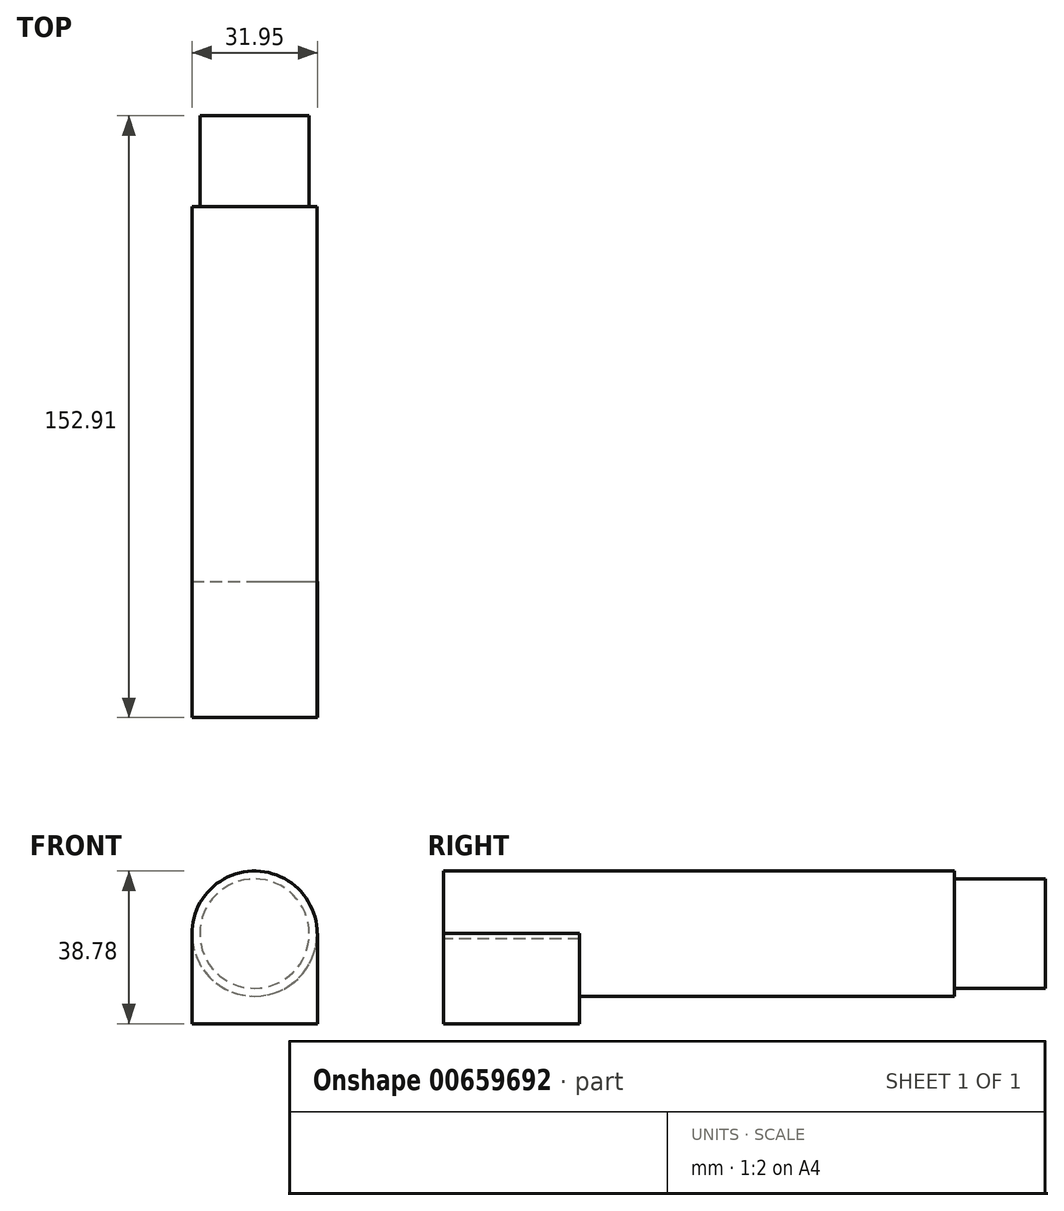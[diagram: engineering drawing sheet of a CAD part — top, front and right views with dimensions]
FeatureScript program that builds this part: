
annotation { "Feature Type Name" : "Feature", "Feature Type Description" : "" }
export const myFeature = defineFeature(function(context is Context, id is Id, definition is map)
    precondition{}
    {
        {
            var Q0;
            Q0=qCreatedBy(makeId("Front.planeOp"),FACE);
            var sketch = newSketch(context, id + "F0", { "sketchPlane" : qUnion([Q0])});
            skCircle(sketch, "E0", {"center": v(0, 0) * mm, "radius": 15.9 * mm});
            skSolve(sketch);
        }
        {
            var Q0;
            Q0 = qSketchRegion(id + "F0", true);
            extrude(context, id + "F1", {"entities" : qUnion([Q0]), "oppositeDirection" : true, "depth" : 129.8 * mm, "offsetDistance" : 25.4 * mm});
        }
        {
            var Q0;
            Q0=qCreatedBy(makeId("Front.planeOp"),FACE);
            var sketch = newSketch(context, id + "F2", { "sketchPlane" : qUnion([Q0])});
            skLineSegment(sketch, "E1.bottom", {"start": v(-15.85, -22.88) * mm, "end": v(16.05, -22.88) * mm});
            skLineSegment(sketch, "E1.top", {"start": v(-15.85, 0) * mm, "end": v(16.05, 0) * mm});
            skLineSegment(sketch, "E1.left", {"start": v(-15.85, -22.88) * mm, "end": v(-15.85, 0) * mm});
            skLineSegment(sketch, "E1.right", {"start": v(16.05, -22.88) * mm, "end": v(16.05, 0) * mm});
            skSolve(sketch);
        }
        {
            var Q0;
            Q0 = qSketchRegion(id + "F2", true);
            extrude(context, id + "F3", {"entities" : qUnion([Q0]), "operationType" : NewBodyOperationType.ADD, "oppositeDirection" : true, "depth" : 34.54 * mm, "offsetDistance" : 25.4 * mm});
        }
        {
            var Q0;
            Q0=qCreatedBy(makeId("Front.planeOp"),FACE);
            var sketch = newSketch(context, id + "F4", { "sketchPlane" : qUnion([Q0])});
            skCircle(sketch, "E2", {"center": v(0, 0) * mm, "radius": 13.9 * mm});
            skSolve(sketch);
        }
        {
            var Q0;
            Q0 = qSketchRegion(id + "F4", true);
            extrude(context, id + "F5", {"entities" : qUnion([Q0]), "operationType" : NewBodyOperationType.ADD, "oppositeDirection" : true, "depth" : 152.9 * mm, "offsetDistance" : 25.4 * mm});
        }
    });
